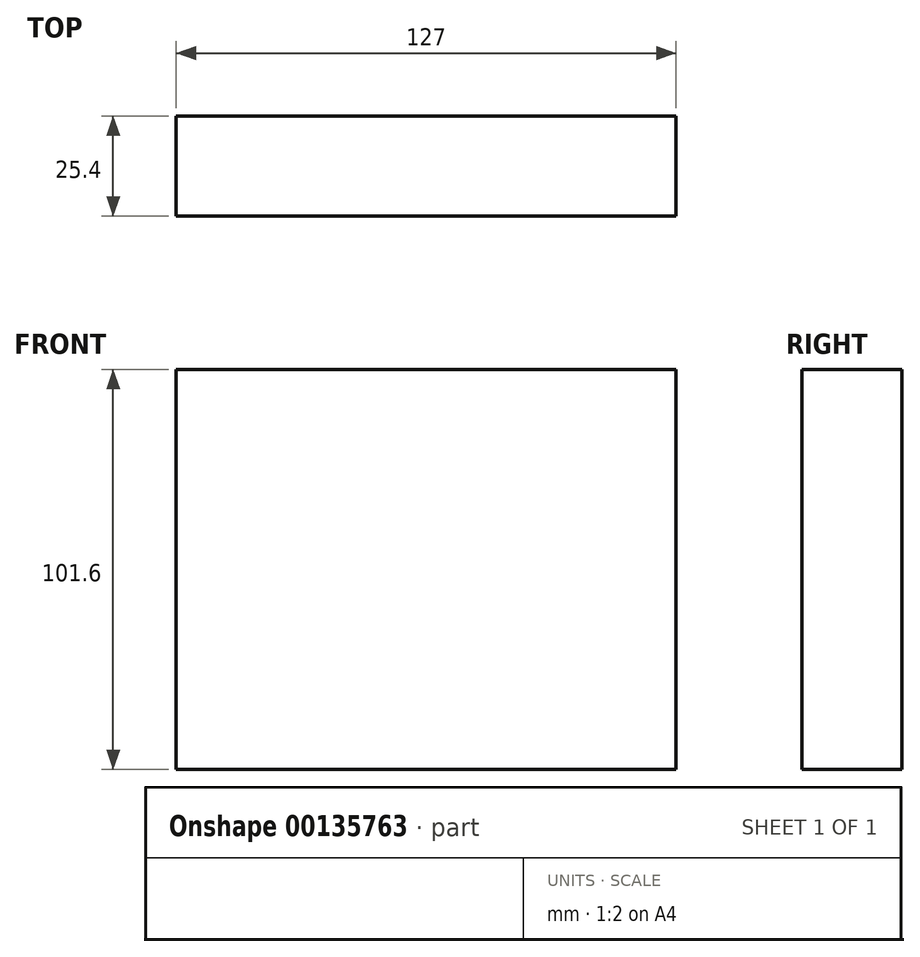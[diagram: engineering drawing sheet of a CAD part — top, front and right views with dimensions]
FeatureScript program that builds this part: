
annotation { "Feature Type Name" : "Feature", "Feature Type Description" : "" }
export const myFeature = defineFeature(function(context is Context, id is Id, definition is map)
    precondition{}
    {
        {
            var Q0;
            Q0=qCreatedBy(makeId("Front.planeOp"),FACE);
            var sketch = newSketch(context, id + "F0", { "sketchPlane" : qUnion([Q0])});
            skLineSegment(sketch, "E0.bottom", {"start": v(63.5, 50.8) * mm, "end": v(-63.5, 50.8) * mm});
            skLineSegment(sketch, "E0.top", {"start": v(63.5, -50.8) * mm, "end": v(-63.5, -50.8) * mm});
            skLineSegment(sketch, "E0.left", {"start": v(63.5, 50.8) * mm, "end": v(63.5, -50.8) * mm});
            skLineSegment(sketch, "E0.right", {"start": v(-63.5, 50.8) * mm, "end": v(-63.5, -50.8) * mm});
            skPoint(sketch, "E0.middle", {"position": v(0, 0) * mm});
            skSolve(sketch);
        }
        {
            var Q0;
            Q0=makeQuery(id+"F0.imprint","IMPRINT",FACE,{"disambiguationData":[TD([[makeQuery(id+"F0.imprint","IMPRINT",EDGE,{"derivedFrom":sQuery(id+"F0.wireOp",EDGE,"E0.bottom")}),1.0]])]});
            extrude(context, id + "F1", {"entities" : qUnion([Q0]), "endBound" : BoundingType.SYMMETRIC, "depth" : 25.4 * mm});
        }
    });
